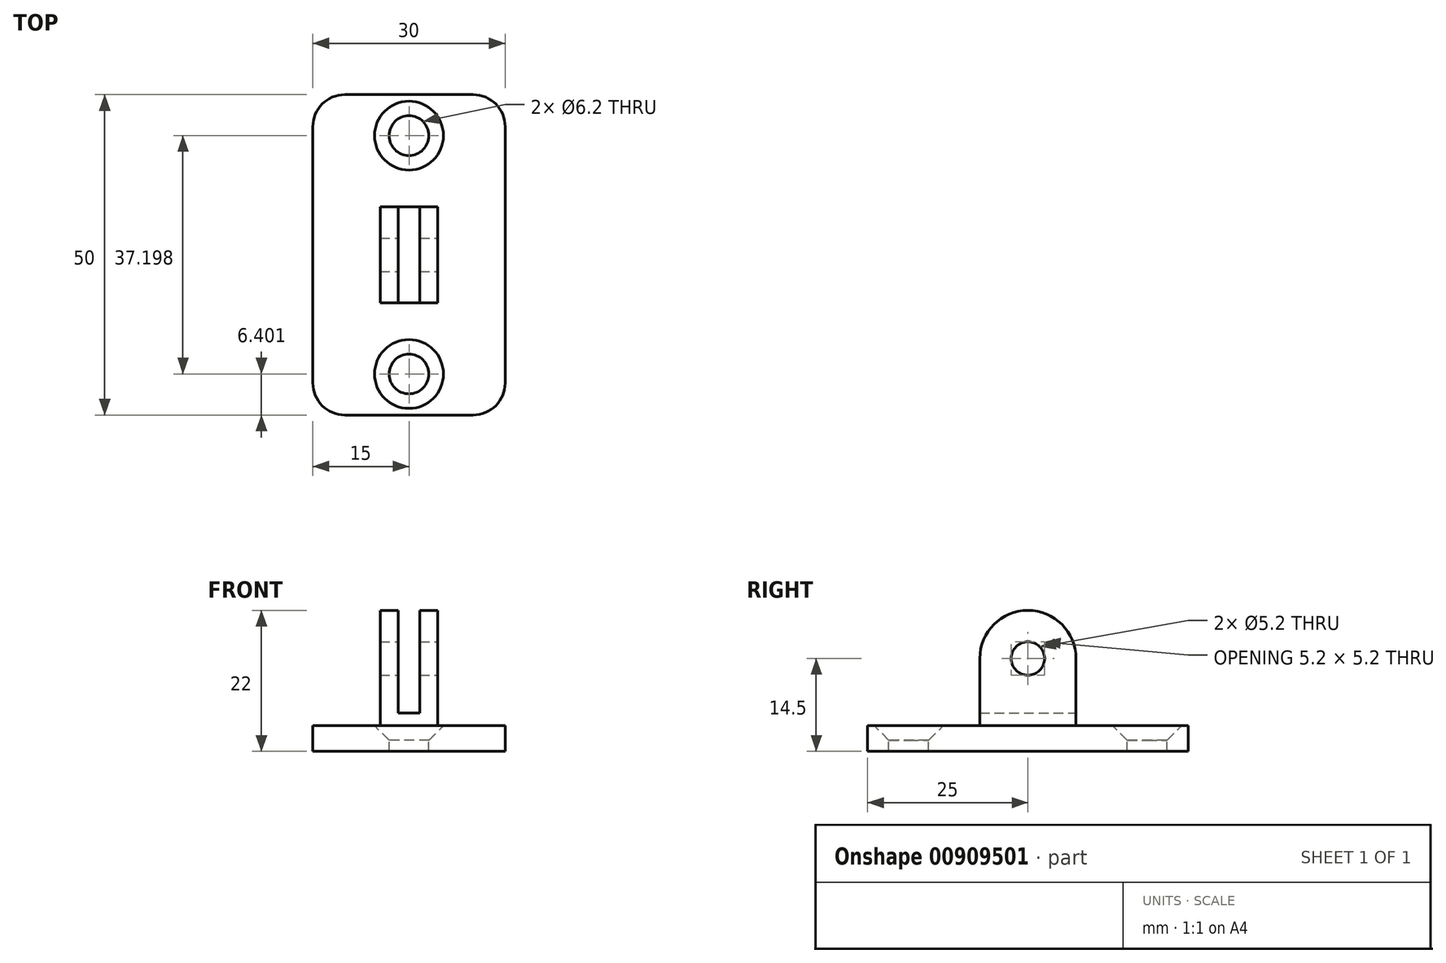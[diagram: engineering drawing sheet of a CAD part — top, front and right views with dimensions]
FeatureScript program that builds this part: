
annotation { "Feature Type Name" : "Feature", "Feature Type Description" : "" }
export const myFeature = defineFeature(function(context is Context, id is Id, definition is map)
    precondition{}
    {
        {
            var Q0;
            Q0=qCreatedBy(makeId("Top.planeOp"),FACE);
            var sketch = newSketch(context, id + "F0", { "sketchPlane" : qUnion([Q0])});
            skLineSegment(sketch, "E0.bottom", {"start": v(15, 25) * mm, "end": v(-15, 25) * mm});
            skLineSegment(sketch, "E0.top", {"start": v(15, -25) * mm, "end": v(-15, -25) * mm});
            skLineSegment(sketch, "E0.left", {"start": v(15, 25) * mm, "end": v(15, -25) * mm});
            skLineSegment(sketch, "E0.right", {"start": v(-15, 25) * mm, "end": v(-15, -25) * mm});
            skPoint(sketch, "E0.middle", {"position": v(0, 0) * mm});
            skSolve(sketch);
        }
        {
            var Q0;
            Q0=makeQuery(id+"F0.imprint","IMPRINT",FACE,{"disambiguationData":[TD([[makeQuery(id+"F0.imprint","IMPRINT",EDGE,{"derivedFrom":sQuery(id+"F0.wireOp",EDGE,"E0.bottom")}),1.0]])]});
            extrude(context, id + "F1", {"entities" : qUnion([Q0]), "oppositeDirection" : true, "depth" : 4 * mm, "offsetDistance" : 25 * mm});
        }
        {
            var Q0;
            Q0=qCreatedBy(makeId("Top.planeOp"),FACE);
            var sketch = newSketch(context, id + "F2", { "sketchPlane" : qUnion([Q0])});
            skLineSegment(sketch, "E1.bottom", {"start": v(4.5, 7.5) * mm, "end": v(-4.5, 7.5) * mm});
            skLineSegment(sketch, "E1.top", {"start": v(4.5, -7.5) * mm, "end": v(-4.5, -7.5) * mm});
            skLineSegment(sketch, "E1.left", {"start": v(4.5, 7.5) * mm, "end": v(4.5, -7.5) * mm});
            skLineSegment(sketch, "E1.right", {"start": v(-4.5, 7.5) * mm, "end": v(-4.5, -7.5) * mm});
            skPoint(sketch, "E1.middle", {"position": v(0, 0) * mm});
            skSolve(sketch);
        }
        {
            var Q0;
            Q0 = qSketchRegion(id + "F2", true);
            extrude(context, id + "F3", {"entities" : qUnion([Q0]), "operationType" : NewBodyOperationType.ADD, "depth" : 18 * mm, "offsetDistance" : 25 * mm});
        }
        {
            var Q0;
            Q0=makeQuery(id+"F3.opExtrude","SWEPT_FACE",FACE,{"disambiguationData":[OSD([sQuery(id+"F2.wireOp",EDGE,"E1.top")])]});
            var sketch = newSketch(context, id + "F4", { "sketchPlane" : qUnion([Q0])});
            skLineSegment(sketch, "E2.bottom", {"start": v(1.7, 18.42) * mm, "end": v(-1.7, 18.42) * mm});
            skLineSegment(sketch, "E2.top", {"start": v(1.7, 0) * mm, "end": v(-1.7, 0) * mm});
            skLineSegment(sketch, "E2.left", {"start": v(1.7, 18.42) * mm, "end": v(1.7, 0) * mm});
            skLineSegment(sketch, "E2.right", {"start": v(-1.7, 18.42) * mm, "end": v(-1.7, 0) * mm});
            skPoint(sketch, "E2.middle", {"position": v(0, 9.21) * mm});
            skPoint(sketch, "E2.middle.positionSnap0", {"position": v(0, 0) * mm});
            skPoint(sketch, "E2.centerSnap0", {"position": v(0, 0) * mm});
            skSolve(sketch);
        }
        {
            var Q0;
            Q0 = qSketchRegion(id + "F4", true);
            extrude(context, id + "F5", {"entities" : qUnion([Q0]), "operationType" : NewBodyOperationType.REMOVE, "endBound" : BoundingType.THROUGH_ALL, "oppositeDirection" : true, "depth" : 25 * mm, "offsetDistance" : 25 * mm});
        }
        {
            var Q0;
            Q0=makeQuery(id+"F3.opExtrude","SWEPT_FACE",FACE,{"disambiguationData":[OSD([sQuery(id+"F2.wireOp",EDGE,"E1.left")])]});
            var sketch = newSketch(context, id + "F6", { "sketchPlane" : qUnion([Q0])});
            skArc(sketch, "E3", {"start": v(7.5, 10.5) * mm, "mid": v(0, 18) * mm, "end": v(-7.5, 10.5) * mm});
            skLineSegment(sketch, "E4", {"start": v(0, 0) * mm, "end": v(0, 14.03) * mm, "construction": true});
            skPoint(sketch, "E5", {"position": v(0, 7.02) * mm});
            skLineSegment(sketch, "E6", {"start": v(-7.5, 10.5) * mm, "end": v(-7.5, 18.7) * mm});
            skLineSegment(sketch, "E7", {"start": v(-7.5, 18.7) * mm, "end": v(7.5, 18.7) * mm});
            skLineSegment(sketch, "E8", {"start": v(7.5, 18.7) * mm, "end": v(7.5, 10.5) * mm});
            skSolve(sketch);
        }
        {
            var Q0;
            Q0 = qSketchRegion(id + "F6", true);
            extrude(context, id + "F7", {"entities" : qUnion([Q0]), "operationType" : NewBodyOperationType.REMOVE, "endBound" : BoundingType.THROUGH_ALL, "oppositeDirection" : true, "depth" : 25 * mm, "offsetDistance" : 25 * mm});
        }
        {
            var Q0;
            Q0=qCreatedBy(makeId("Top.planeOp"),FACE);
            var sketch = newSketch(context, id + "F8", { "sketchPlane" : qUnion([Q0])});
            skLineSegment(sketch, "E9.bottom", {"start": v(-4.5, 7.5) * mm, "end": v(4.5, 7.5) * mm});
            skLineSegment(sketch, "E9.top", {"start": v(-4.5, -7.5) * mm, "end": v(4.5, -7.5) * mm});
            skLineSegment(sketch, "E9.left", {"start": v(-4.5, 7.5) * mm, "end": v(-4.5, -7.5) * mm});
            skLineSegment(sketch, "E9.right", {"start": v(4.5, 7.5) * mm, "end": v(4.5, -7.5) * mm});
            skSolve(sketch);
        }
        {
            var Q0;
            Q0 = qSketchRegion(id + "F8", true);
            extrude(context, id + "F9", {"entities" : qUnion([Q0]), "operationType" : NewBodyOperationType.ADD, "depth" : 2 * mm, "offsetDistance" : 25 * mm});
        }
        {
            var Q0;
            Q0=makeQuery(id+"F3.opExtrude","CAP_EDGE",EDGE,{"disambiguationData":[OSD([sQuery(id+"F2.wireOp",EDGE,"E1.left")])],"isStart":true});
            var Q1;
            {var subQ1=sQuery(id+"F2.wireOp",EDGE,"E1.top");var subQ4=makeQuery(id+"F3.opExtrude","CAP_EDGE",EDGE,{"disambiguationData":[OSD([subQ1])],"isStart":true});Q1=makeQuery(id+"F9.boolean.opBoolean","MERGE",EDGE,{"derivedFrom":[makeQuery(id+"F5.boolean.opBoolean","SPLIT",EDGE,{"disambiguationData":[TD([makeQuery(id+"F3.opExtrude","SWEPT_FACE",FACE,{"disambiguationData":[OSD([sQuery(id+"F2.wireOp",EDGE,"E1.left")])]})])],"derivedFrom":subQ4}),makeQuery(id+"F5.boolean.opBoolean","SPLIT",EDGE,{"disambiguationData":[TD([makeQuery(id+"F3.opExtrude","SWEPT_FACE",FACE,{"disambiguationData":[OSD([sQuery(id+"F2.wireOp",EDGE,"E1.right")])]})])],"derivedFrom":subQ4}),makeQuery(id+"F9.opExtrude","CAP_EDGE",EDGE,{"disambiguationData":[OSD([sQuery(id+"F8.wireOp",EDGE,"E9.top")])],"isStart":true})]});}
            var Q2;
            Q2=makeQuery(id+"F3.opExtrude","CAP_EDGE",EDGE,{"disambiguationData":[OSD([sQuery(id+"F2.wireOp",EDGE,"E1.right")])],"isStart":true});
            var Q3;
            {var subQ1=sQuery(id+"F2.wireOp",EDGE,"E1.bottom");var subQ4=makeQuery(id+"F3.opExtrude","CAP_EDGE",EDGE,{"disambiguationData":[OSD([subQ1])],"isStart":true});Q3=makeQuery(id+"F9.boolean.opBoolean","MERGE",EDGE,{"derivedFrom":[makeQuery(id+"F5.boolean.opBoolean","SPLIT",EDGE,{"disambiguationData":[TD([makeQuery(id+"F3.opExtrude","SWEPT_FACE",FACE,{"disambiguationData":[OSD([sQuery(id+"F2.wireOp",EDGE,"E1.left")])]})])],"derivedFrom":subQ4}),makeQuery(id+"F5.boolean.opBoolean","SPLIT",EDGE,{"disambiguationData":[TD([makeQuery(id+"F3.opExtrude","SWEPT_FACE",FACE,{"disambiguationData":[OSD([sQuery(id+"F2.wireOp",EDGE,"E1.right")])]})])],"derivedFrom":subQ4}),makeQuery(id+"F9.opExtrude","CAP_EDGE",EDGE,{"disambiguationData":[OSD([sQuery(id+"F8.wireOp",EDGE,"E9.bottom")])],"isStart":true})]});}
            var Q4;
            Q4=makeQuery(id+"F1.opExtrude","SWEPT_EDGE",EDGE,{"disambiguationData":[OSD([sQuery(id+"F0.wireOp",EDGE,"E0.top"),sQuery(id+"F0.wireOp",EDGE,"E0.right")])]});
            var Q5;
            Q5=makeQuery(id+"F1.opExtrude","SWEPT_EDGE",EDGE,{"disambiguationData":[OSD([sQuery(id+"F0.wireOp",EDGE,"E0.top"),sQuery(id+"F0.wireOp",EDGE,"E0.left")])]});
            var Q6;
            Q6=makeQuery(id+"F1.opExtrude","SWEPT_EDGE",EDGE,{"disambiguationData":[OSD([sQuery(id+"F0.wireOp",EDGE,"E0.bottom"),sQuery(id+"F0.wireOp",EDGE,"E0.left")])]});
            var Q7;
            Q7=makeQuery(id+"F1.opExtrude","SWEPT_EDGE",EDGE,{"disambiguationData":[OSD([sQuery(id+"F0.wireOp",EDGE,"E0.bottom"),sQuery(id+"F0.wireOp",EDGE,"E0.right")])]});
            fillet(context, id + "F10", {"entities" : qUnion([Q0, Q1, Q2, Q3, Q4, Q5, Q6, Q7]), "radius" : 5 * mm, "tangentPropagation" : true, "allowEdgeOverflow" : false});
        }
        {
            var Q0;
            Q0=makeQuery(id+"F3.opExtrude","SWEPT_FACE",FACE,{"disambiguationData":[OSD([sQuery(id+"F2.wireOp",EDGE,"E1.left")])]});
            var sketch = newSketch(context, id + "F11", { "sketchPlane" : qUnion([Q0])});
            skPoint(sketch, "E10", {"position": v(0, 10.5) * mm});
            skSolve(sketch);
        }
        {
            var Q0;
            Q0=sQuery(id+"F11.wireOp",VERTEX,"E10");
            var Q1;
            Q1=makeQuery(id+"F1.opExtrude","SWEPT_BODY",BODY,{"disambiguationData":[OSD([sQuery(id+"F0.wireOp",EDGE,"E0.bottom"),sQuery(id+"F0.wireOp",EDGE,"E0.top"),sQuery(id+"F0.wireOp",EDGE,"E0.left"),sQuery(id+"F0.wireOp",EDGE,"E0.right")])]});
            hole(context, id + "F12", {"style" : HoleStyle.SIMPLE, "endStyle" : HoleEndStyle.THROUGH, "holeDiameter" : 5.2 * mm, "majorDiameter" : 5 * mm, "isTappedThrough" : true, "tappedDepth" : 12 * mm, "tapClearance" : 3, "locations" : qUnion([Q0]), "scope" : qUnion([Q1])});
        }
        {
            var Q0;
            Q0=makeQuery(id+"F5.boolean.opBoolean","MERGE",FACE,{"derivedFrom":[makeQuery(id+"F1.opExtrude","CAP_FACE",FACE,{"disambiguationData":[OSD([sQuery(id+"F0.wireOp",EDGE,"E0.bottom"),sQuery(id+"F0.wireOp",EDGE,"E0.top"),sQuery(id+"F0.wireOp",EDGE,"E0.left"),sQuery(id+"F0.wireOp",EDGE,"E0.right")])],"isStart":true})],"fromTools":[makeQuery(id+"F5.opExtrude","SWEPT_FACE",FACE,{"disambiguationData":[OSD([sQuery(id+"F4.wireOp",EDGE,"E2.top")])]})]});
            var sketch = newSketch(context, id + "F13", { "sketchPlane" : qUnion([Q0])});
            skPoint(sketch, "E11", {"position": v(0, -18.6) * mm});
            skPoint(sketch, "E12", {"position": v(0, 18.6) * mm});
            skSolve(sketch);
        }
        {
            var Q0;
            Q0=sQuery(id+"F13.wireOp",VERTEX,"E11");
            var Q1;
            Q1=sQuery(id+"F13.wireOp",VERTEX,"E12");
            var Q2;
            Q2=makeQuery(id+"F1.opExtrude","SWEPT_BODY",BODY,{"disambiguationData":[OSD([sQuery(id+"F0.wireOp",EDGE,"E0.bottom"),sQuery(id+"F0.wireOp",EDGE,"E0.top"),sQuery(id+"F0.wireOp",EDGE,"E0.left"),sQuery(id+"F0.wireOp",EDGE,"E0.right")])]});
            hole(context, id + "F14", {"style" : HoleStyle.C_SINK, "endStyle" : HoleEndStyle.THROUGH, "holeDiameter" : 6.2 * mm, "cSinkDiameter" : 10.75 * mm, "cSinkAngle" : 90 * degree, "majorDiameter" : 5 * mm, "isTappedThrough" : true, "tappedDepth" : 12 * mm, "tapClearance" : 3, "locations" : qUnion([Q0, Q1]), "scope" : qUnion([Q2])});
        }
    });
